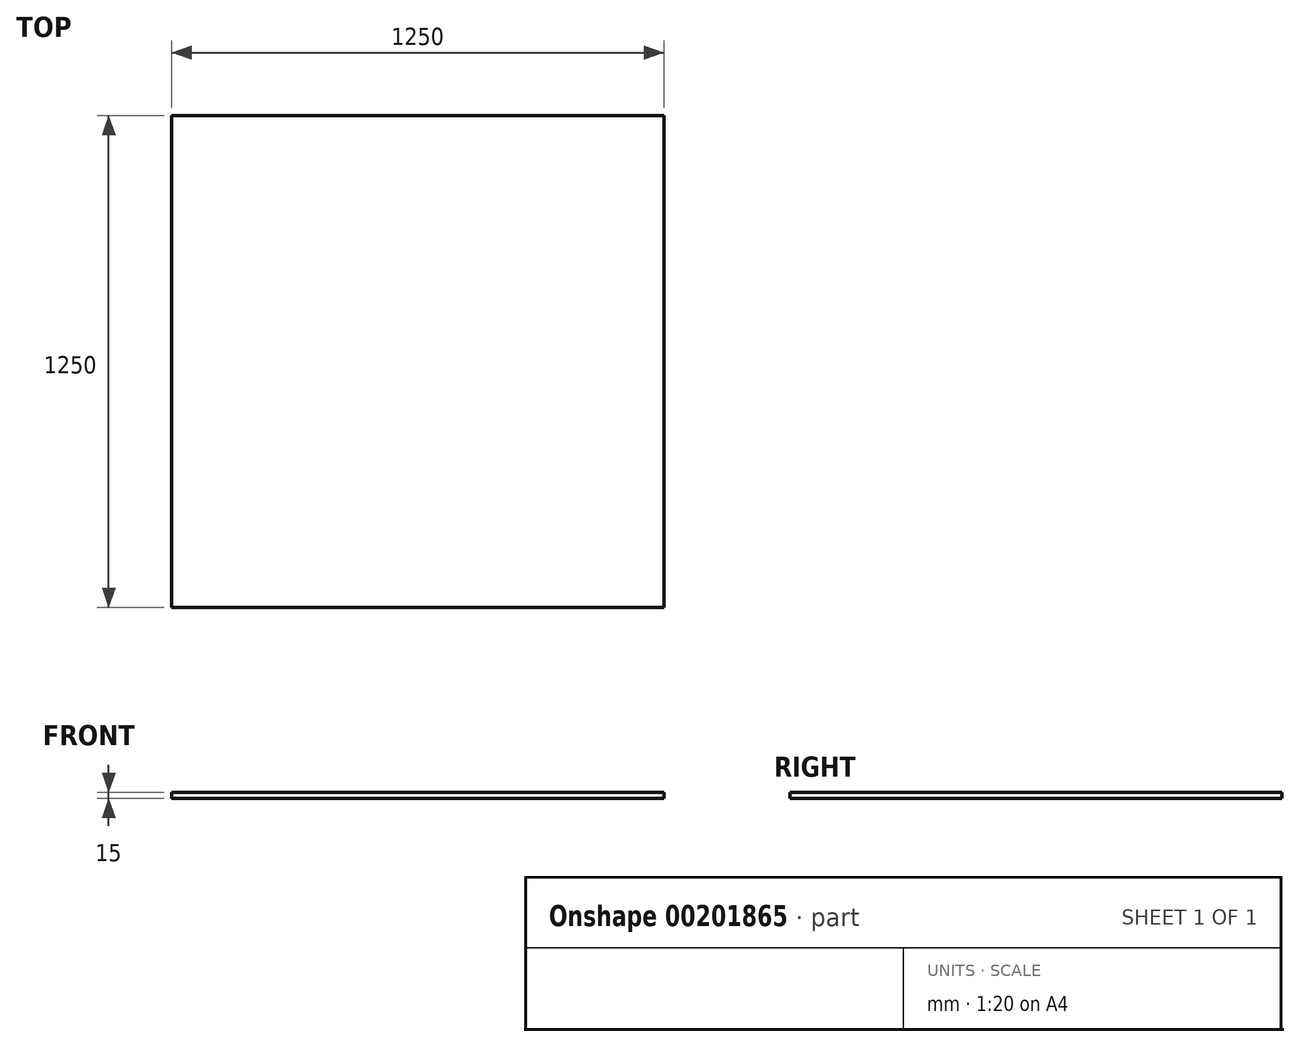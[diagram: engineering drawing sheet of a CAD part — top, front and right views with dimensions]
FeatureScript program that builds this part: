
annotation { "Feature Type Name" : "Feature", "Feature Type Description" : "" }
export const myFeature = defineFeature(function(context is Context, id is Id, definition is map)
    precondition{}
    {
        {
            var Q0;
            Q0=qCreatedBy(makeId("Top.planeOp"),FACE);
            var sketch = newSketch(context, id + "F0", { "sketchPlane" : qUnion([Q0])});
            skLineSegment(sketch, "E0.bottom", {"start": v(-625, 625) * mm, "end": v(625, 625) * mm});
            skLineSegment(sketch, "E0.top", {"start": v(-625, -625) * mm, "end": v(625, -625) * mm});
            skLineSegment(sketch, "E0.left", {"start": v(-625, 625) * mm, "end": v(-625, -625) * mm});
            skLineSegment(sketch, "E0.right", {"start": v(625, 625) * mm, "end": v(625, -625) * mm});
            skPoint(sketch, "E0.middle", {"position": v(0, 0) * mm});
            skSolve(sketch);
        }
        {
            var Q0;
            Q0=makeQuery(id+"F0.imprint","IMPRINT",FACE,{"disambiguationData":[TD([[makeQuery(id+"F0.imprint","IMPRINT",EDGE,{"derivedFrom":sQuery(id+"F0.wireOp",EDGE,"E0.bottom")}),-1.0]])]});
            extrude(context, id + "F1", {"entities" : qUnion([Q0]), "depth" : 15 * mm});
        }
    });
